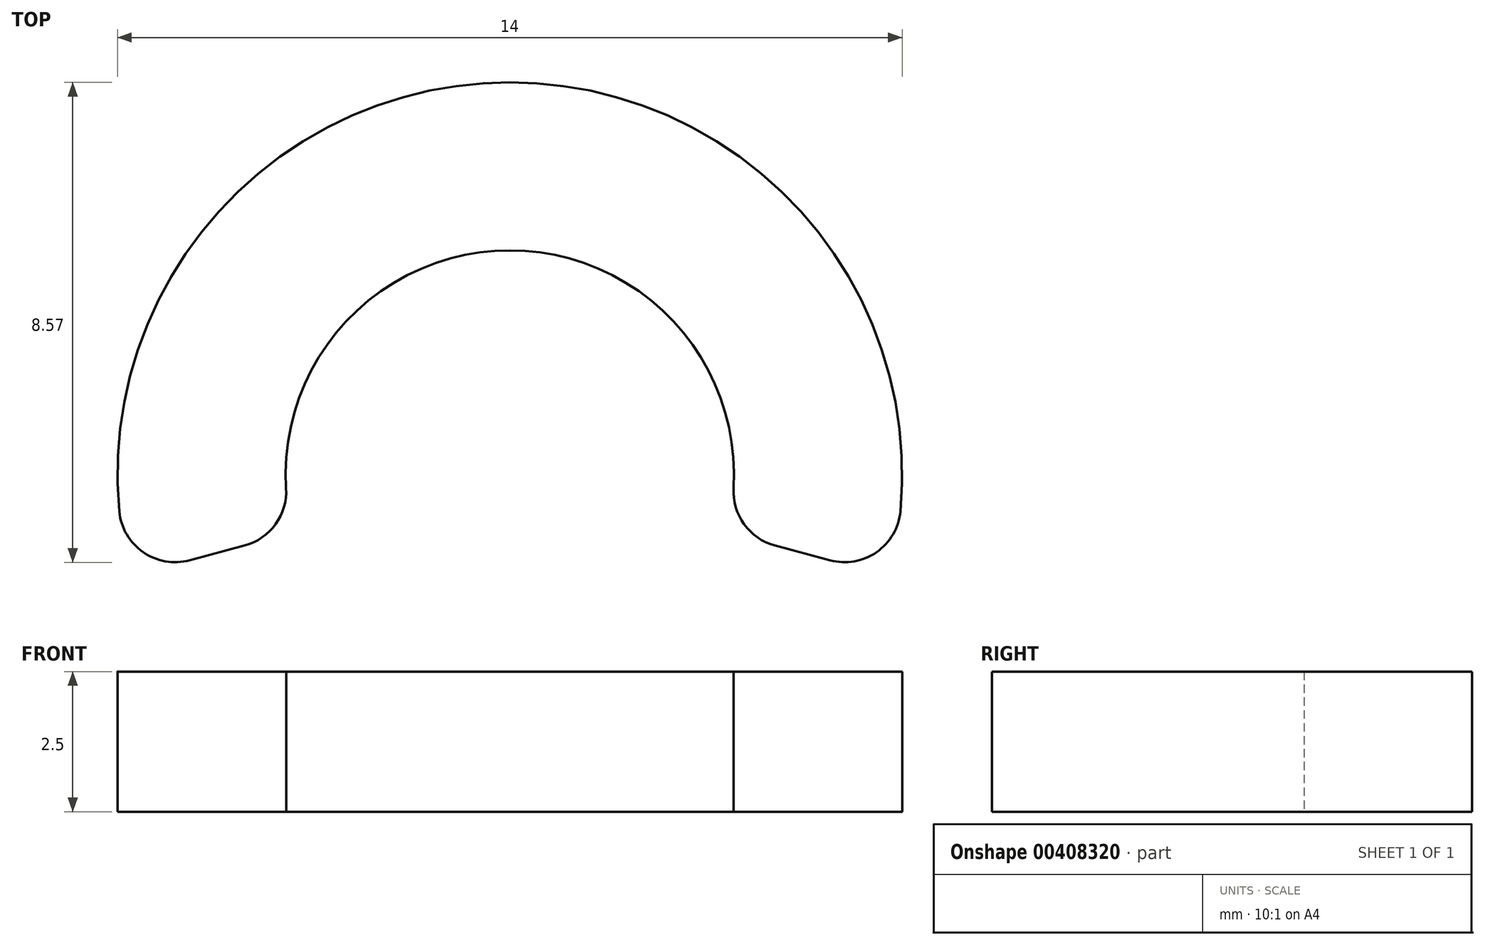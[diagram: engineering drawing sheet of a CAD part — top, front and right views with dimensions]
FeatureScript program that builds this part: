
annotation { "Feature Type Name" : "Feature", "Feature Type Description" : "" }
export const myFeature = defineFeature(function(context is Context, id is Id, definition is map)
    precondition{}
    {
        {
            var Q0;
            Q0=qCreatedBy(makeId("Top.planeOp"),FACE);
            var sketch = newSketch(context, id + "F0", { "sketchPlane" : qUnion([Q0])});
            skArc(sketch, "E0", {"start": v(6.76, -1.81) * mm, "mid": v(0, 7) * mm, "end": v(-6.76, -1.81) * mm});
            skArc(sketch, "E1", {"start": v(3.86, -1.04) * mm, "mid": v(0, 4) * mm, "end": v(-3.86, -1.04) * mm});
            skLineSegment(sketch, "E2", {"start": v(-6.76, -1.81) * mm, "end": v(-3.86, -1.04) * mm});
            skLineSegment(sketch, "E3", {"start": v(3.86, -1.04) * mm, "end": v(6.76, -1.81) * mm});
            skSolve(sketch);
        }
        {
            var Q0;
            Q0 = qSketchRegion(id + "F0", true);
            extrude(context, id + "F1", {"entities" : qUnion([Q0]), "depth" : 2.5 * mm});
        }
        {
            var Q0;
            Q0=makeQuery(id+"F1.opExtrude","SWEPT_EDGE",EDGE,{"disambiguationData":[OSD([sQuery(id+"F0.wireOp",EDGE,"E0"),sQuery(id+"F0.wireOp",EDGE,"E2")])]});
            var Q1;
            Q1=makeQuery(id+"F1.opExtrude","SWEPT_EDGE",EDGE,{"disambiguationData":[OSD([sQuery(id+"F0.wireOp",EDGE,"E1"),sQuery(id+"F0.wireOp",EDGE,"E2")])]});
            var Q2;
            Q2=makeQuery(id+"F1.opExtrude","SWEPT_EDGE",EDGE,{"disambiguationData":[OSD([sQuery(id+"F0.wireOp",EDGE,"E1"),sQuery(id+"F0.wireOp",EDGE,"E3")])]});
            var Q3;
            Q3=makeQuery(id+"F1.opExtrude","SWEPT_EDGE",EDGE,{"disambiguationData":[OSD([sQuery(id+"F0.wireOp",EDGE,"E0"),sQuery(id+"F0.wireOp",EDGE,"E3")])]});
            fillet(context, id + "F2", {"entities" : qUnion([Q0, Q1, Q2, Q3]), "radius" : 1 * mm, "tangentPropagation" : true, "allowEdgeOverflow" : false});
        }
    });
